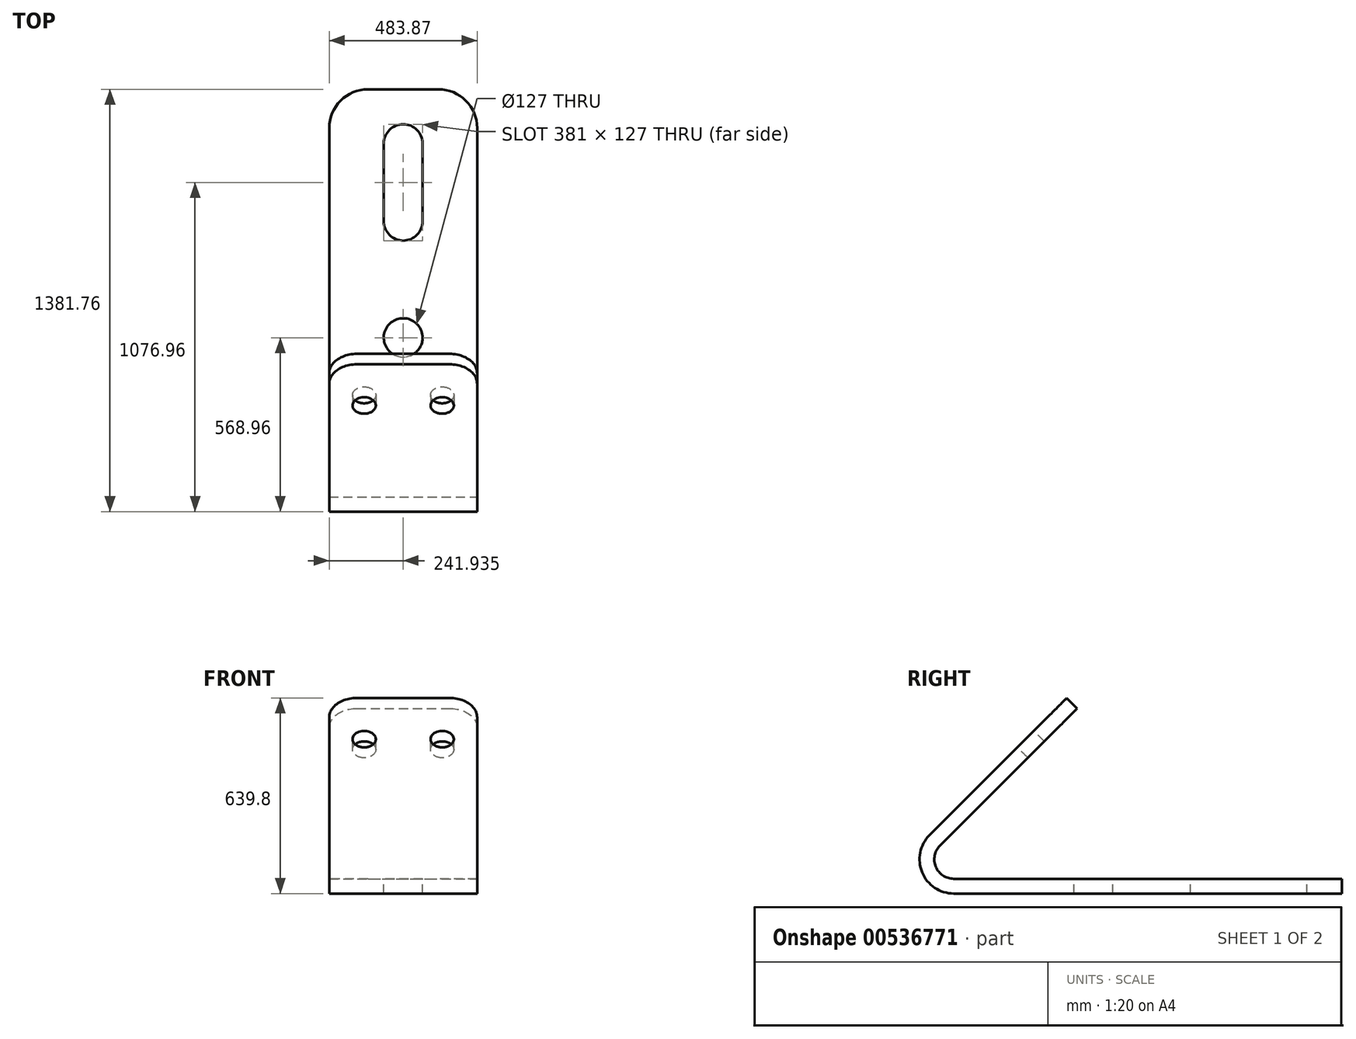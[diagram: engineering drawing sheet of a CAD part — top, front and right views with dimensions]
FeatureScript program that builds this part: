
annotation { "Feature Type Name" : "Feature", "Feature Type Description" : "" }
export const myFeature = defineFeature(function(context is Context, id is Id, definition is map)
    precondition{}
    {
        {
            var Q0;
            Q0=qCreatedBy(makeId("Right.planeOp"),FACE);
            var sketch = newSketch(context, id + "F0", { "sketchPlane" : qUnion([Q0])});
            skLineSegment(sketch, "E0", {"start": v(0, 0) * mm, "end": v(812.8, 0) * mm});
            skLineSegment(sketch, "E1", {"start": v(812.8, 0) * mm, "end": v(812.8, -48.26) * mm});
            skLineSegment(sketch, "E2", {"start": v(812.8, -48.26) * mm, "end": v(-457.2, -48.26) * mm});
            skArc(sketch, "E3", {"start": v(-536.23, 142.53) * mm, "mid": v(-560.45, 20.73) * mm, "end": v(-457.2, -48.26) * mm});
            skLineSegment(sketch, "E4", {"start": v(-536.23, 142.53) * mm, "end": v(-87.21, 591.54) * mm});
            skLineSegment(sketch, "E5", {"start": v(0, 0) * mm, "end": v(-457.2, 0) * mm});
            skArc(sketch, "E6", {"start": v(-502.1, 108.4) * mm, "mid": v(-515.87, 39.2) * mm, "end": v(-457.2, 0) * mm});
            skLineSegment(sketch, "E7", {"start": v(-502.1, 108.4) * mm, "end": v(-53.09, 557.41) * mm});
            skLineSegment(sketch, "E8", {"start": v(-87.21, 591.54) * mm, "end": v(-53.09, 557.41) * mm});
            skSolve(sketch);
        }
        {
            var Q0;
            Q0=makeQuery(id+"F0.imprint","IMPRINT",FACE,{"disambiguationData":[TD([[makeQuery(id+"F0.imprint","IMPRINT",EDGE,{"derivedFrom":sQuery(id+"F0.wireOp",EDGE,"E0")}),-1.0]])]});
            extrude(context, id + "F1", {"entities" : qUnion([Q0]), "oppositeDirection" : true, "depth" : 483.87 * mm, "offsetDistance" : 25.4 * mm});
        }
        {
            var Q0;
            Q0=makeQuery(id+"F1.opExtrude","SWEPT_FACE",FACE,{"disambiguationData":[OSD([sQuery(id+"F0.wireOp",EDGE,"E0"),sQuery(id+"F0.wireOp",EDGE,"E5")])]});
            var sketch = newSketch(context, id + "F2", { "sketchPlane" : qUnion([Q0])});
            skLineSegment(sketch, "E9", {"start": v(-483.87, 812.8) * mm, "end": v(-356.87, 812.8) * mm});
            skLineSegment(sketch, "E10", {"start": v(-241.94, 812.8) * mm, "end": v(-241.94, -457.2) * mm, "construction": true});
            skCircle(sketch, "E11", {"center": v(-241.94, 0) * mm, "radius": 63.5 * mm});
            skLineSegment(sketch, "E12", {"start": v(-178.44, 635) * mm, "end": v(-178.44, 381) * mm});
            skLineSegment(sketch, "E13", {"start": v(-305.44, 635) * mm, "end": v(-305.44, 381) * mm});
            skLineSegment(sketch, "E14", {"start": v(-483.87, 812.8) * mm, "end": v(-483.87, 685.8) * mm});
            skLineSegment(sketch, "E15", {"start": v(0, 812.8) * mm, "end": v(0, 685.8) * mm});
            skArc(sketch, "E16", {"start": v(-356.87, 812.8) * mm, "mid": v(-446.67, 775.6) * mm, "end": v(-483.87, 685.8) * mm});
            skArc(sketch, "E17", {"start": v(0, 685.8) * mm, "mid": v(-37.2, 775.6) * mm, "end": v(-127, 812.8) * mm});
            skArc(sketch, "E18", {"start": v(-305.44, 381) * mm, "mid": v(-241.94, 317.5) * mm, "end": v(-178.44, 381) * mm});
            skArc(sketch, "E19", {"start": v(-178.44, 381) * mm, "mid": v(-241.94, 444.5) * mm, "end": v(-305.44, 381) * mm, "construction": true});
            skArc(sketch, "E20", {"start": v(-178.44, 635) * mm, "mid": v(-241.94, 698.5) * mm, "end": v(-305.44, 635) * mm});
            skArc(sketch, "E21", {"start": v(-305.44, 635) * mm, "mid": v(-241.94, 571.5) * mm, "end": v(-178.44, 635) * mm, "construction": true});
            skLineSegment(sketch, "E22", {"start": v(0, 685.8) * mm, "end": v(0, -457.2) * mm, "construction": true});
            skLineSegment(sketch, "E23", {"start": v(-127, 812.8) * mm, "end": v(0, 812.8) * mm});
            skLineSegment(sketch, "E24", {"start": v(-356.87, 812.8) * mm, "end": v(-127, 812.8) * mm, "construction": true});
            skLineSegment(sketch, "E25", {"start": v(-483.87, 685.8) * mm, "end": v(-483.87, -457.2) * mm, "construction": true});
            skSolve(sketch);
        }
        {
            var Q0;
            Q0 = qSketchRegion(id + "F2", true);
            var Q1;
            Q1=makeQuery(id+"F1.opExtrude","SWEPT_FACE",FACE,{"disambiguationData":[OSD([sQuery(id+"F0.wireOp",EDGE,"E2")])]});
            extrude(context, id + "F3", {"entities" : qUnion([Q0]), "operationType" : NewBodyOperationType.REMOVE, "endBound" : BoundingType.UP_TO_SURFACE, "oppositeDirection" : true, "depth" : 25.4 * mm, "endBoundEntityFace" : qUnion([Q1]), "offsetDistance" : 25.4 * mm});
        }
        {
            var Q0;
            Q0=makeQuery(id+"F1.opExtrude","SWEPT_FACE",FACE,{"disambiguationData":[OSD([sQuery(id+"F0.wireOp",EDGE,"E4")])]});
            var sketch = newSketch(context, id + "F4", { "sketchPlane" : qUnion([Q0])});
            skLineSegment(sketch, "E26", {"start": v(-483.87, -278.39) * mm, "end": v(-483.87, 266.8) * mm, "construction": true});
            skLineSegment(sketch, "E27", {"start": v(-483.87, 356.61) * mm, "end": v(-394.07, 356.61) * mm});
            skLineSegment(sketch, "E28", {"start": v(0, 356.61) * mm, "end": v(0, 266.8) * mm});
            skCircle(sketch, "E29", {"center": v(-369.57, 166.11) * mm, "radius": 38.1 * mm});
            skCircle(sketch, "E30", {"center": v(-114.3, 166.11) * mm, "radius": 38.1 * mm});
            skArc(sketch, "E31", {"start": v(0, 266.8) * mm, "mid": v(-26.3, 330.3) * mm, "end": v(-89.8, 356.61) * mm});
            skArc(sketch, "E32", {"start": v(-394.07, 356.61) * mm, "mid": v(-457.57, 330.3) * mm, "end": v(-483.87, 266.8) * mm});
            skLineSegment(sketch, "E33", {"start": v(-394.07, 356.61) * mm, "end": v(-89.8, 356.61) * mm, "construction": true});
            skLineSegment(sketch, "E34", {"start": v(-483.87, 266.8) * mm, "end": v(-483.87, 266.8) * mm});
            skLineSegment(sketch, "E35", {"start": v(-89.8, 356.61) * mm, "end": v(0, 356.61) * mm});
            skLineSegment(sketch, "E36", {"start": v(0, 266.8) * mm, "end": v(0, -278.39) * mm, "construction": true});
            skLineSegment(sketch, "E37", {"start": v(-483.87, 266.8) * mm, "end": v(-483.87, 356.61) * mm});
            skSolve(sketch);
        }
        {
            var Q0;
            Q0 = qSketchRegion(id + "F4", true);
            var Q1;
            Q1=makeQuery(id+"F1.opExtrude","SWEPT_FACE",FACE,{"disambiguationData":[OSD([sQuery(id+"F0.wireOp",EDGE,"E7")])]});
            extrude(context, id + "F5", {"entities" : qUnion([Q0]), "operationType" : NewBodyOperationType.REMOVE, "endBound" : BoundingType.UP_TO_SURFACE, "oppositeDirection" : true, "depth" : 25.4 * mm, "endBoundEntityFace" : qUnion([Q1]), "offsetDistance" : 25.4 * mm});
        }
    });
